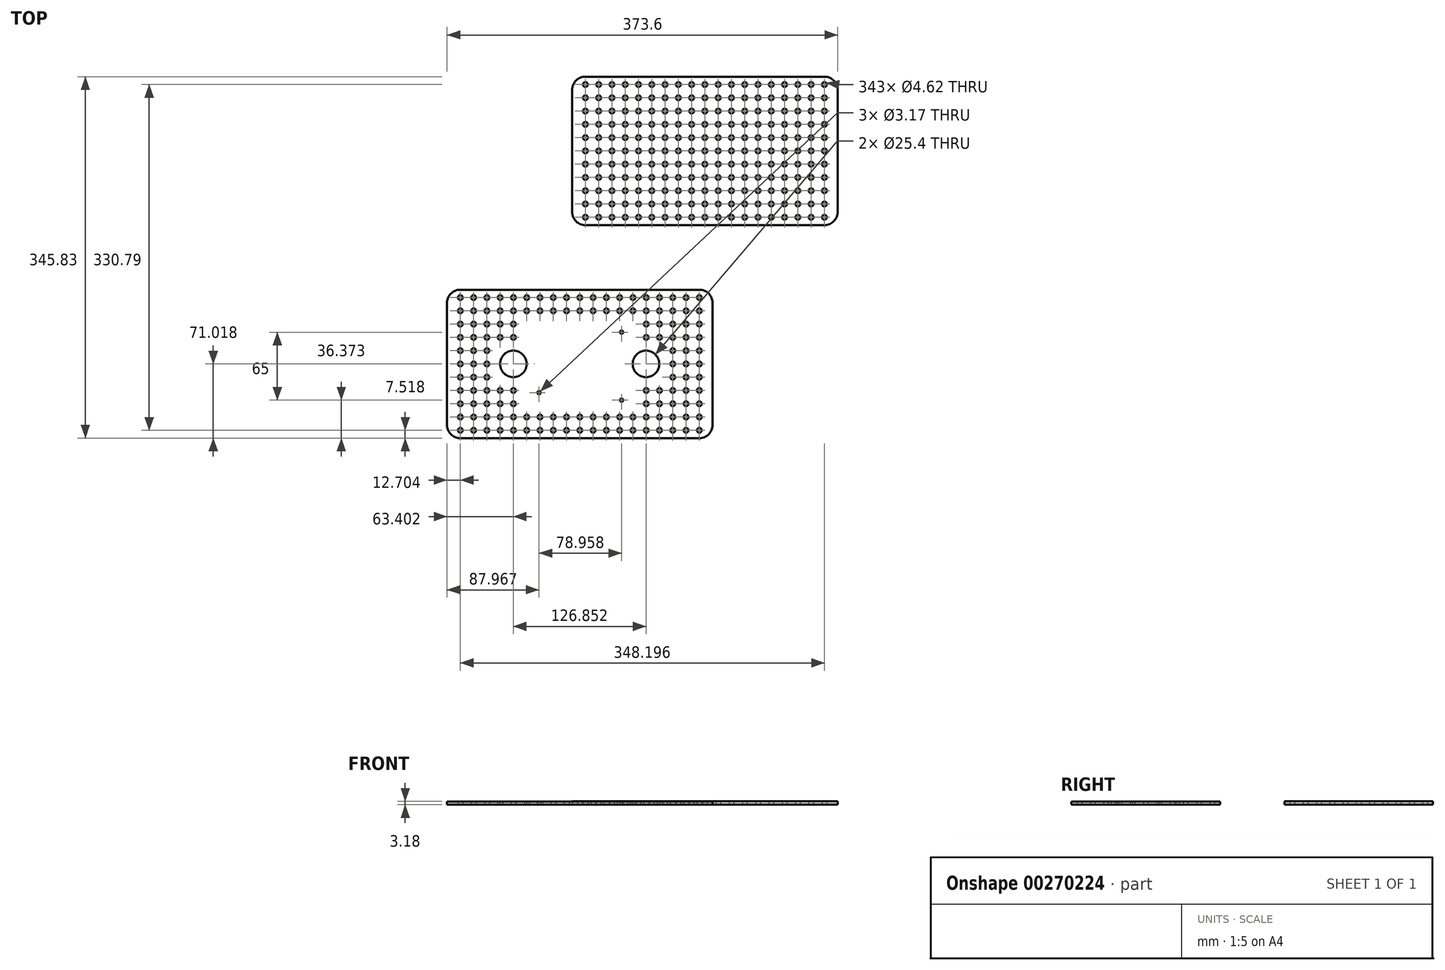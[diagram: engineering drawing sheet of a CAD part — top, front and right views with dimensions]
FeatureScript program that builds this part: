
annotation { "Feature Type Name" : "Feature", "Feature Type Description" : "" }
export const myFeature = defineFeature(function(context is Context, id is Id, definition is map)
    precondition{}
    {
        {
            var Q0;
            Q0=qCreatedBy(makeId("Top.planeOp"),FACE);
            var sketch = newSketch(context, id + "F0", { "sketchPlane" : qUnion([Q0])});
            skLineSegment(sketch, "E0.bottom", {"start": v(12.7, 0) * mm, "end": v(241.3, 0) * mm});
            skLineSegment(sketch, "E0.top", {"start": v(12.7, 142.04) * mm, "end": v(241.3, 142.04) * mm});
            skLineSegment(sketch, "E0.left", {"start": v(0, 12.7) * mm, "end": v(0, 129.34) * mm});
            skLineSegment(sketch, "E0.right", {"start": v(254, 12.7) * mm, "end": v(254, 129.34) * mm});
            skCircle(sketch, "E1", {"center": v(12.7, 134.52) * mm, "radius": 2.31 * mm});
            skCircle(sketch, "E2.1.0.0", {"center": v(25.4, 134.52) * mm, "radius": 2.31 * mm});
            skCircle(sketch, "E2.2.0.0", {"center": v(38.1, 134.52) * mm, "radius": 2.31 * mm});
            skCircle(sketch, "E2.3.0.0", {"center": v(50.8, 134.52) * mm, "radius": 2.31 * mm});
            skCircle(sketch, "E2.4.0.0", {"center": v(63.5, 134.52) * mm, "radius": 2.31 * mm});
            skCircle(sketch, "E2.5.0.0", {"center": v(76.2, 134.52) * mm, "radius": 2.31 * mm});
            skCircle(sketch, "E2.6.0.0", {"center": v(88.9, 134.52) * mm, "radius": 2.31 * mm});
            skCircle(sketch, "E2.7.0.0", {"center": v(101.6, 134.52) * mm, "radius": 2.31 * mm});
            skCircle(sketch, "E2.8.0.0", {"center": v(114.3, 134.52) * mm, "radius": 2.31 * mm});
            skCircle(sketch, "E2.9.0.0", {"center": v(127, 134.52) * mm, "radius": 2.31 * mm});
            skCircle(sketch, "E2.10.0.0", {"center": v(139.7, 134.52) * mm, "radius": 2.31 * mm});
            skLineSegment(sketch, "E2.direction1", {"start": v(12.7, 134.52) * mm, "end": v(25.4, 134.52) * mm, "construction": true});
            skCircle(sketch, "E3.0.11.0", {"center": v(152.4, 134.52) * mm, "radius": 2.31 * mm});
            skCircle(sketch, "E3.0.12.0", {"center": v(165.1, 134.52) * mm, "radius": 2.31 * mm});
            skCircle(sketch, "E3.0.13.0", {"center": v(177.8, 134.52) * mm, "radius": 2.31 * mm});
            skCircle(sketch, "E3.0.14.0", {"center": v(190.5, 134.52) * mm, "radius": 2.31 * mm});
            skCircle(sketch, "E3.0.15.0", {"center": v(203.2, 134.52) * mm, "radius": 2.31 * mm});
            skCircle(sketch, "E3.0.16.0", {"center": v(215.9, 134.52) * mm, "radius": 2.31 * mm});
            skCircle(sketch, "E3.0.17.0", {"center": v(228.6, 134.52) * mm, "radius": 2.31 * mm});
            skCircle(sketch, "E3.0.18.0", {"center": v(241.3, 134.52) * mm, "radius": 2.31 * mm});
            skCircle(sketch, "E4.0.1.0", {"center": v(76.2, 121.82) * mm, "radius": 2.31 * mm});
            skCircle(sketch, "E4.0.2.0", {"center": v(76.2, 109.12) * mm, "radius": 2.31 * mm});
            skCircle(sketch, "E4.0.3.0", {"center": v(76.2, 96.42) * mm, "radius": 2.31 * mm});
            skCircle(sketch, "E4.0.4.0", {"center": v(76.2, 83.72) * mm, "radius": 2.31 * mm});
            skCircle(sketch, "E4.0.5.0", {"center": v(76.2, 71.02) * mm, "radius": 2.31 * mm});
            skCircle(sketch, "E4.0.6.0", {"center": v(76.2, 58.32) * mm, "radius": 2.31 * mm});
            skCircle(sketch, "E4.0.7.0", {"center": v(76.2, 45.62) * mm, "radius": 2.31 * mm});
            skCircle(sketch, "E4.0.8.0", {"center": v(76.2, 32.92) * mm, "radius": 2.31 * mm});
            skCircle(sketch, "E4.0.9.0", {"center": v(76.2, 20.22) * mm, "radius": 2.31 * mm});
            skCircle(sketch, "E4.0.10.0", {"center": v(76.2, 7.52) * mm, "radius": 2.31 * mm});
            skCircle(sketch, "E4.1.1.0", {"center": v(88.9, 121.82) * mm, "radius": 2.31 * mm});
            skCircle(sketch, "E4.1.2.0", {"center": v(88.9, 109.12) * mm, "radius": 2.31 * mm});
            skCircle(sketch, "E4.1.3.0", {"center": v(88.9, 96.42) * mm, "radius": 2.31 * mm});
            skCircle(sketch, "E4.1.4.0", {"center": v(88.9, 83.72) * mm, "radius": 2.31 * mm});
            skCircle(sketch, "E4.1.5.0", {"center": v(88.9, 71.02) * mm, "radius": 2.31 * mm});
            skCircle(sketch, "E4.1.6.0", {"center": v(88.9, 58.32) * mm, "radius": 2.31 * mm});
            skCircle(sketch, "E4.1.7.0", {"center": v(88.9, 45.62) * mm, "radius": 2.31 * mm});
            skCircle(sketch, "E4.1.8.0", {"center": v(88.9, 32.92) * mm, "radius": 2.31 * mm});
            skCircle(sketch, "E4.1.9.0", {"center": v(88.9, 20.22) * mm, "radius": 2.31 * mm});
            skCircle(sketch, "E4.1.10.0", {"center": v(88.9, 7.52) * mm, "radius": 2.31 * mm});
            skCircle(sketch, "E4.2.1.0", {"center": v(101.6, 121.82) * mm, "radius": 2.31 * mm});
            skCircle(sketch, "E4.2.2.0", {"center": v(101.6, 109.12) * mm, "radius": 2.31 * mm});
            skCircle(sketch, "E4.2.3.0", {"center": v(101.6, 96.42) * mm, "radius": 2.31 * mm});
            skCircle(sketch, "E4.2.4.0", {"center": v(101.6, 83.72) * mm, "radius": 2.31 * mm});
            skCircle(sketch, "E4.2.5.0", {"center": v(101.6, 71.02) * mm, "radius": 2.31 * mm});
            skCircle(sketch, "E4.2.6.0", {"center": v(101.6, 58.32) * mm, "radius": 2.31 * mm});
            skCircle(sketch, "E4.2.7.0", {"center": v(101.6, 45.62) * mm, "radius": 2.31 * mm});
            skCircle(sketch, "E4.2.8.0", {"center": v(101.6, 32.92) * mm, "radius": 2.31 * mm});
            skCircle(sketch, "E4.2.9.0", {"center": v(101.6, 20.22) * mm, "radius": 2.31 * mm});
            skCircle(sketch, "E4.2.10.0", {"center": v(101.6, 7.52) * mm, "radius": 2.31 * mm});
            skCircle(sketch, "E4.3.1.0", {"center": v(114.3, 121.82) * mm, "radius": 2.31 * mm});
            skCircle(sketch, "E4.3.2.0", {"center": v(114.3, 109.12) * mm, "radius": 2.31 * mm});
            skCircle(sketch, "E4.3.3.0", {"center": v(114.3, 96.42) * mm, "radius": 2.31 * mm});
            skCircle(sketch, "E4.3.4.0", {"center": v(114.3, 83.72) * mm, "radius": 2.31 * mm});
            skCircle(sketch, "E4.3.5.0", {"center": v(114.3, 71.02) * mm, "radius": 2.31 * mm});
            skCircle(sketch, "E4.3.6.0", {"center": v(114.3, 58.32) * mm, "radius": 2.31 * mm});
            skCircle(sketch, "E4.3.7.0", {"center": v(114.3, 45.62) * mm, "radius": 2.31 * mm});
            skCircle(sketch, "E4.3.8.0", {"center": v(114.3, 32.92) * mm, "radius": 2.31 * mm});
            skCircle(sketch, "E4.3.9.0", {"center": v(114.3, 20.22) * mm, "radius": 2.31 * mm});
            skCircle(sketch, "E4.3.10.0", {"center": v(114.3, 7.52) * mm, "radius": 2.31 * mm});
            skCircle(sketch, "E4.4.1.0", {"center": v(127, 121.82) * mm, "radius": 2.31 * mm});
            skCircle(sketch, "E4.4.2.0", {"center": v(127, 109.12) * mm, "radius": 2.31 * mm});
            skCircle(sketch, "E4.4.3.0", {"center": v(127, 96.42) * mm, "radius": 2.31 * mm});
            skCircle(sketch, "E4.4.4.0", {"center": v(127, 83.72) * mm, "radius": 2.31 * mm});
            skCircle(sketch, "E4.4.5.0", {"center": v(127, 71.02) * mm, "radius": 2.31 * mm});
            skCircle(sketch, "E4.4.6.0", {"center": v(127, 58.32) * mm, "radius": 2.31 * mm});
            skCircle(sketch, "E4.4.7.0", {"center": v(127, 45.62) * mm, "radius": 2.31 * mm});
            skCircle(sketch, "E4.4.8.0", {"center": v(127, 32.92) * mm, "radius": 2.31 * mm});
            skCircle(sketch, "E4.4.9.0", {"center": v(127, 20.22) * mm, "radius": 2.31 * mm});
            skCircle(sketch, "E4.4.10.0", {"center": v(127, 7.52) * mm, "radius": 2.31 * mm});
            skCircle(sketch, "E4.5.1.0", {"center": v(139.7, 121.82) * mm, "radius": 2.31 * mm});
            skCircle(sketch, "E4.5.2.0", {"center": v(139.7, 109.12) * mm, "radius": 2.31 * mm});
            skCircle(sketch, "E4.5.3.0", {"center": v(139.7, 96.42) * mm, "radius": 2.31 * mm});
            skCircle(sketch, "E4.5.4.0", {"center": v(139.7, 83.72) * mm, "radius": 2.31 * mm});
            skCircle(sketch, "E4.5.5.0", {"center": v(139.7, 71.02) * mm, "radius": 2.31 * mm});
            skCircle(sketch, "E4.5.6.0", {"center": v(139.7, 58.32) * mm, "radius": 2.31 * mm});
            skCircle(sketch, "E4.5.7.0", {"center": v(139.7, 45.62) * mm, "radius": 2.31 * mm});
            skCircle(sketch, "E4.5.8.0", {"center": v(139.7, 32.92) * mm, "radius": 2.31 * mm});
            skCircle(sketch, "E4.5.9.0", {"center": v(139.7, 20.22) * mm, "radius": 2.31 * mm});
            skCircle(sketch, "E4.5.10.0", {"center": v(139.7, 7.52) * mm, "radius": 2.31 * mm});
            skCircle(sketch, "E4.6.1.0", {"center": v(152.4, 121.82) * mm, "radius": 2.31 * mm});
            skCircle(sketch, "E4.6.2.0", {"center": v(152.4, 109.12) * mm, "radius": 2.31 * mm});
            skCircle(sketch, "E4.6.3.0", {"center": v(152.4, 96.42) * mm, "radius": 2.31 * mm});
            skCircle(sketch, "E4.6.4.0", {"center": v(152.4, 83.72) * mm, "radius": 2.31 * mm});
            skCircle(sketch, "E4.6.5.0", {"center": v(152.4, 71.02) * mm, "radius": 2.31 * mm});
            skCircle(sketch, "E4.6.6.0", {"center": v(152.4, 58.32) * mm, "radius": 2.31 * mm});
            skCircle(sketch, "E4.6.7.0", {"center": v(152.4, 45.62) * mm, "radius": 2.31 * mm});
            skCircle(sketch, "E4.6.8.0", {"center": v(152.4, 32.92) * mm, "radius": 2.31 * mm});
            skCircle(sketch, "E4.6.9.0", {"center": v(152.4, 20.22) * mm, "radius": 2.31 * mm});
            skCircle(sketch, "E4.6.10.0", {"center": v(152.4, 7.52) * mm, "radius": 2.31 * mm});
            skCircle(sketch, "E4.7.1.0", {"center": v(165.1, 121.82) * mm, "radius": 2.31 * mm});
            skCircle(sketch, "E4.7.2.0", {"center": v(165.1, 109.12) * mm, "radius": 2.31 * mm});
            skCircle(sketch, "E4.7.3.0", {"center": v(165.1, 96.42) * mm, "radius": 2.31 * mm});
            skCircle(sketch, "E4.7.4.0", {"center": v(165.1, 83.72) * mm, "radius": 2.31 * mm});
            skCircle(sketch, "E4.7.5.0", {"center": v(165.1, 71.02) * mm, "radius": 2.31 * mm});
            skCircle(sketch, "E4.7.6.0", {"center": v(165.1, 58.32) * mm, "radius": 2.31 * mm});
            skCircle(sketch, "E4.7.7.0", {"center": v(165.1, 45.62) * mm, "radius": 2.31 * mm});
            skCircle(sketch, "E4.7.8.0", {"center": v(165.1, 32.92) * mm, "radius": 2.31 * mm});
            skCircle(sketch, "E4.7.9.0", {"center": v(165.1, 20.22) * mm, "radius": 2.31 * mm});
            skCircle(sketch, "E4.7.10.0", {"center": v(165.1, 7.52) * mm, "radius": 2.31 * mm});
            skCircle(sketch, "E4.8.1.0", {"center": v(177.8, 121.82) * mm, "radius": 2.31 * mm});
            skCircle(sketch, "E4.8.2.0", {"center": v(177.8, 109.12) * mm, "radius": 2.31 * mm});
            skCircle(sketch, "E4.8.3.0", {"center": v(177.8, 96.42) * mm, "radius": 2.31 * mm});
            skCircle(sketch, "E4.8.4.0", {"center": v(177.8, 83.72) * mm, "radius": 2.31 * mm});
            skCircle(sketch, "E4.8.5.0", {"center": v(177.8, 71.02) * mm, "radius": 2.31 * mm});
            skCircle(sketch, "E4.8.6.0", {"center": v(177.8, 58.32) * mm, "radius": 2.31 * mm});
            skCircle(sketch, "E4.8.7.0", {"center": v(177.8, 45.62) * mm, "radius": 2.31 * mm});
            skCircle(sketch, "E4.8.8.0", {"center": v(177.8, 32.92) * mm, "radius": 2.31 * mm});
            skCircle(sketch, "E4.8.9.0", {"center": v(177.8, 20.22) * mm, "radius": 2.31 * mm});
            skCircle(sketch, "E4.8.10.0", {"center": v(177.8, 7.52) * mm, "radius": 2.31 * mm});
            skCircle(sketch, "E4.9.1.0", {"center": v(190.5, 121.82) * mm, "radius": 2.31 * mm});
            skCircle(sketch, "E4.9.2.0", {"center": v(190.5, 109.12) * mm, "radius": 2.31 * mm});
            skCircle(sketch, "E4.9.3.0", {"center": v(190.5, 96.42) * mm, "radius": 2.31 * mm});
            skCircle(sketch, "E4.9.4.0", {"center": v(190.5, 83.72) * mm, "radius": 2.31 * mm});
            skCircle(sketch, "E4.9.5.0", {"center": v(190.5, 71.02) * mm, "radius": 2.31 * mm});
            skCircle(sketch, "E4.9.6.0", {"center": v(190.5, 58.32) * mm, "radius": 2.31 * mm});
            skCircle(sketch, "E4.9.7.0", {"center": v(190.5, 45.62) * mm, "radius": 2.31 * mm});
            skCircle(sketch, "E4.9.8.0", {"center": v(190.5, 32.92) * mm, "radius": 2.31 * mm});
            skCircle(sketch, "E4.9.9.0", {"center": v(190.5, 20.22) * mm, "radius": 2.31 * mm});
            skCircle(sketch, "E4.9.10.0", {"center": v(190.5, 7.52) * mm, "radius": 2.31 * mm});
            skCircle(sketch, "E4.10.1.0", {"center": v(203.2, 121.82) * mm, "radius": 2.31 * mm});
            skCircle(sketch, "E4.10.2.0", {"center": v(203.2, 109.12) * mm, "radius": 2.31 * mm});
            skCircle(sketch, "E4.10.3.0", {"center": v(203.2, 96.42) * mm, "radius": 2.31 * mm});
            skCircle(sketch, "E4.10.4.0", {"center": v(203.2, 83.72) * mm, "radius": 2.31 * mm});
            skCircle(sketch, "E4.10.5.0", {"center": v(203.2, 71.02) * mm, "radius": 2.31 * mm});
            skCircle(sketch, "E4.10.6.0", {"center": v(203.2, 58.32) * mm, "radius": 2.31 * mm});
            skCircle(sketch, "E4.10.7.0", {"center": v(203.2, 45.62) * mm, "radius": 2.31 * mm});
            skCircle(sketch, "E4.10.8.0", {"center": v(203.2, 32.92) * mm, "radius": 2.31 * mm});
            skCircle(sketch, "E4.10.9.0", {"center": v(203.2, 20.22) * mm, "radius": 2.31 * mm});
            skCircle(sketch, "E4.10.10.0", {"center": v(203.2, 7.52) * mm, "radius": 2.31 * mm});
            skCircle(sketch, "E4.11.1.0", {"center": v(215.9, 121.82) * mm, "radius": 2.31 * mm});
            skCircle(sketch, "E4.11.2.0", {"center": v(215.9, 109.12) * mm, "radius": 2.31 * mm});
            skCircle(sketch, "E4.11.3.0", {"center": v(215.9, 96.42) * mm, "radius": 2.31 * mm});
            skCircle(sketch, "E4.11.4.0", {"center": v(215.9, 83.72) * mm, "radius": 2.31 * mm});
            skCircle(sketch, "E4.11.5.0", {"center": v(215.9, 71.02) * mm, "radius": 2.31 * mm});
            skCircle(sketch, "E4.11.6.0", {"center": v(215.9, 58.32) * mm, "radius": 2.31 * mm});
            skCircle(sketch, "E4.11.7.0", {"center": v(215.9, 45.62) * mm, "radius": 2.31 * mm});
            skCircle(sketch, "E4.11.8.0", {"center": v(215.9, 32.92) * mm, "radius": 2.31 * mm});
            skCircle(sketch, "E4.11.9.0", {"center": v(215.9, 20.22) * mm, "radius": 2.31 * mm});
            skCircle(sketch, "E4.11.10.0", {"center": v(215.9, 7.52) * mm, "radius": 2.31 * mm});
            skCircle(sketch, "E4.12.1.0", {"center": v(228.6, 121.82) * mm, "radius": 2.31 * mm});
            skCircle(sketch, "E4.12.2.0", {"center": v(228.6, 109.12) * mm, "radius": 2.31 * mm});
            skCircle(sketch, "E4.12.3.0", {"center": v(228.6, 96.42) * mm, "radius": 2.31 * mm});
            skCircle(sketch, "E4.12.4.0", {"center": v(228.6, 83.72) * mm, "radius": 2.31 * mm});
            skCircle(sketch, "E4.12.5.0", {"center": v(228.6, 71.02) * mm, "radius": 2.31 * mm});
            skCircle(sketch, "E4.12.6.0", {"center": v(228.6, 58.32) * mm, "radius": 2.31 * mm});
            skCircle(sketch, "E4.12.7.0", {"center": v(228.6, 45.62) * mm, "radius": 2.31 * mm});
            skCircle(sketch, "E4.12.8.0", {"center": v(228.6, 32.92) * mm, "radius": 2.31 * mm});
            skCircle(sketch, "E4.12.9.0", {"center": v(228.6, 20.22) * mm, "radius": 2.31 * mm});
            skCircle(sketch, "E4.12.10.0", {"center": v(228.6, 7.52) * mm, "radius": 2.31 * mm});
            skCircle(sketch, "E4.13.1.0", {"center": v(241.3, 121.82) * mm, "radius": 2.31 * mm});
            skCircle(sketch, "E4.13.2.0", {"center": v(241.3, 109.12) * mm, "radius": 2.31 * mm});
            skCircle(sketch, "E4.13.3.0", {"center": v(241.3, 96.42) * mm, "radius": 2.31 * mm});
            skCircle(sketch, "E4.13.4.0", {"center": v(241.3, 83.72) * mm, "radius": 2.31 * mm});
            skCircle(sketch, "E4.13.5.0", {"center": v(241.3, 71.02) * mm, "radius": 2.31 * mm});
            skCircle(sketch, "E4.13.6.0", {"center": v(241.3, 58.32) * mm, "radius": 2.31 * mm});
            skCircle(sketch, "E4.13.7.0", {"center": v(241.3, 45.62) * mm, "radius": 2.31 * mm});
            skCircle(sketch, "E4.13.8.0", {"center": v(241.3, 32.92) * mm, "radius": 2.31 * mm});
            skCircle(sketch, "E4.13.9.0", {"center": v(241.3, 20.22) * mm, "radius": 2.31 * mm});
            skCircle(sketch, "E4.13.10.0", {"center": v(241.3, 7.52) * mm, "radius": 2.31 * mm});
            skLineSegment(sketch, "E4.direction1", {"start": v(76.2, 134.52) * mm, "end": v(88.9, 134.52) * mm, "construction": true});
            skLineSegment(sketch, "E4.direction2", {"start": v(76.2, 134.52) * mm, "end": v(76.2, 121.82) * mm, "construction": true});
            skCircle(sketch, "E5.0.1.0", {"center": v(12.7, 121.82) * mm, "radius": 2.31 * mm});
            skCircle(sketch, "E5.0.2.0", {"center": v(12.7, 109.12) * mm, "radius": 2.31 * mm});
            skCircle(sketch, "E5.0.3.0", {"center": v(12.7, 96.42) * mm, "radius": 2.31 * mm});
            skCircle(sketch, "E5.0.4.0", {"center": v(12.7, 83.72) * mm, "radius": 2.31 * mm});
            skCircle(sketch, "E5.0.5.0", {"center": v(12.7, 71.02) * mm, "radius": 2.31 * mm});
            skCircle(sketch, "E5.0.6.0", {"center": v(12.7, 58.32) * mm, "radius": 2.31 * mm});
            skCircle(sketch, "E5.0.7.0", {"center": v(12.7, 45.62) * mm, "radius": 2.31 * mm});
            skCircle(sketch, "E5.0.8.0", {"center": v(12.7, 32.92) * mm, "radius": 2.31 * mm});
            skCircle(sketch, "E5.0.9.0", {"center": v(12.7, 20.22) * mm, "radius": 2.31 * mm});
            skCircle(sketch, "E5.0.10.0", {"center": v(12.7, 7.52) * mm, "radius": 2.31 * mm});
            skCircle(sketch, "E5.1.1.0", {"center": v(25.4, 121.82) * mm, "radius": 2.31 * mm});
            skCircle(sketch, "E5.1.2.0", {"center": v(25.4, 109.12) * mm, "radius": 2.31 * mm});
            skCircle(sketch, "E5.1.3.0", {"center": v(25.4, 96.42) * mm, "radius": 2.31 * mm});
            skCircle(sketch, "E5.1.4.0", {"center": v(25.4, 83.72) * mm, "radius": 2.31 * mm});
            skCircle(sketch, "E5.1.5.0", {"center": v(25.4, 71.02) * mm, "radius": 2.31 * mm});
            skCircle(sketch, "E5.1.6.0", {"center": v(25.4, 58.32) * mm, "radius": 2.31 * mm});
            skCircle(sketch, "E5.1.7.0", {"center": v(25.4, 45.62) * mm, "radius": 2.31 * mm});
            skCircle(sketch, "E5.1.8.0", {"center": v(25.4, 32.92) * mm, "radius": 2.31 * mm});
            skCircle(sketch, "E5.1.9.0", {"center": v(25.4, 20.22) * mm, "radius": 2.31 * mm});
            skCircle(sketch, "E5.1.10.0", {"center": v(25.4, 7.52) * mm, "radius": 2.31 * mm});
            skCircle(sketch, "E5.2.1.0", {"center": v(38.1, 121.82) * mm, "radius": 2.31 * mm});
            skCircle(sketch, "E5.2.2.0", {"center": v(38.1, 109.12) * mm, "radius": 2.31 * mm});
            skCircle(sketch, "E5.2.3.0", {"center": v(38.1, 96.42) * mm, "radius": 2.31 * mm});
            skCircle(sketch, "E5.2.4.0", {"center": v(38.1, 83.72) * mm, "radius": 2.31 * mm});
            skCircle(sketch, "E5.2.5.0", {"center": v(38.1, 71.02) * mm, "radius": 2.31 * mm});
            skCircle(sketch, "E5.2.6.0", {"center": v(38.1, 58.32) * mm, "radius": 2.31 * mm});
            skCircle(sketch, "E5.2.7.0", {"center": v(38.1, 45.62) * mm, "radius": 2.31 * mm});
            skCircle(sketch, "E5.2.8.0", {"center": v(38.1, 32.92) * mm, "radius": 2.31 * mm});
            skCircle(sketch, "E5.2.9.0", {"center": v(38.1, 20.22) * mm, "radius": 2.31 * mm});
            skCircle(sketch, "E5.2.10.0", {"center": v(38.1, 7.52) * mm, "radius": 2.31 * mm});
            skCircle(sketch, "E5.3.1.0", {"center": v(50.8, 121.82) * mm, "radius": 2.31 * mm});
            skCircle(sketch, "E5.3.2.0", {"center": v(50.8, 109.12) * mm, "radius": 2.31 * mm});
            skCircle(sketch, "E5.3.3.0", {"center": v(50.8, 96.42) * mm, "radius": 2.31 * mm});
            skCircle(sketch, "E5.3.4.0", {"center": v(50.8, 83.72) * mm, "radius": 2.31 * mm});
            skCircle(sketch, "E5.3.5.0", {"center": v(50.8, 71.02) * mm, "radius": 2.31 * mm});
            skCircle(sketch, "E5.3.6.0", {"center": v(50.8, 58.32) * mm, "radius": 2.31 * mm});
            skCircle(sketch, "E5.3.7.0", {"center": v(50.8, 45.62) * mm, "radius": 2.31 * mm});
            skCircle(sketch, "E5.3.8.0", {"center": v(50.8, 32.92) * mm, "radius": 2.31 * mm});
            skCircle(sketch, "E5.3.9.0", {"center": v(50.8, 20.22) * mm, "radius": 2.31 * mm});
            skCircle(sketch, "E5.3.10.0", {"center": v(50.8, 7.52) * mm, "radius": 2.31 * mm});
            skCircle(sketch, "E5.4.1.0", {"center": v(63.5, 121.82) * mm, "radius": 2.31 * mm});
            skCircle(sketch, "E5.4.2.0", {"center": v(63.5, 109.12) * mm, "radius": 2.31 * mm});
            skCircle(sketch, "E5.4.3.0", {"center": v(63.5, 96.42) * mm, "radius": 2.31 * mm});
            skCircle(sketch, "E5.4.4.0", {"center": v(63.5, 83.72) * mm, "radius": 2.31 * mm});
            skCircle(sketch, "E5.4.5.0", {"center": v(63.5, 71.02) * mm, "radius": 2.31 * mm});
            skCircle(sketch, "E5.4.6.0", {"center": v(63.5, 58.32) * mm, "radius": 2.31 * mm});
            skCircle(sketch, "E5.4.7.0", {"center": v(63.5, 45.62) * mm, "radius": 2.31 * mm});
            skCircle(sketch, "E5.4.8.0", {"center": v(63.5, 32.92) * mm, "radius": 2.31 * mm});
            skCircle(sketch, "E5.4.9.0", {"center": v(63.5, 20.22) * mm, "radius": 2.31 * mm});
            skCircle(sketch, "E5.4.10.0", {"center": v(63.5, 7.52) * mm, "radius": 2.31 * mm});
            skLineSegment(sketch, "E5.direction2", {"start": v(12.7, 134.52) * mm, "end": v(12.7, 121.82) * mm, "construction": true});
            skLineSegment(sketch, "E6.bottom", {"start": v(-106.9, -203.8) * mm, "end": v(121.7, -203.8) * mm});
            skLineSegment(sketch, "E6.top", {"start": v(-106.9, -61.75) * mm, "end": v(121.7, -61.75) * mm});
            skLineSegment(sketch, "E6.left", {"start": v(-119.6, -191.1) * mm, "end": v(-119.6, -74.45) * mm});
            skLineSegment(sketch, "E6.right", {"start": v(134.4, -191.1) * mm, "end": v(134.4, -74.45) * mm});
            skCircle(sketch, "E7", {"center": v(-106.9, -69.27) * mm, "radius": 2.31 * mm});
            skCircle(sketch, "E8.1.0.0", {"center": v(-94.2, -69.27) * mm, "radius": 2.31 * mm});
            skCircle(sketch, "E8.2.0.0", {"center": v(-81.5, -69.27) * mm, "radius": 2.31 * mm});
            skCircle(sketch, "E8.3.0.0", {"center": v(-68.8, -69.27) * mm, "radius": 2.31 * mm});
            skCircle(sketch, "E8.4.0.0", {"center": v(-56.1, -69.27) * mm, "radius": 2.31 * mm});
            skCircle(sketch, "E8.5.0.0", {"center": v(-43.4, -69.27) * mm, "radius": 2.31 * mm});
            skCircle(sketch, "E8.6.0.0", {"center": v(-30.7, -69.27) * mm, "radius": 2.31 * mm});
            skCircle(sketch, "E8.7.0.0", {"center": v(-18, -69.27) * mm, "radius": 2.31 * mm});
            skCircle(sketch, "E8.8.0.0", {"center": v(-5.3, -69.27) * mm, "radius": 2.31 * mm});
            skCircle(sketch, "E8.9.0.0", {"center": v(7.4, -69.27) * mm, "radius": 2.31 * mm});
            skCircle(sketch, "E8.10.0.0", {"center": v(20.1, -69.27) * mm, "radius": 2.31 * mm});
            skLineSegment(sketch, "E8.direction1", {"start": v(-106.9, -69.27) * mm, "end": v(-94.2, -69.27) * mm, "construction": true});
            skCircle(sketch, "E9.0.11.0", {"center": v(32.8, -69.27) * mm, "radius": 2.31 * mm});
            skCircle(sketch, "E9.0.12.0", {"center": v(45.5, -69.27) * mm, "radius": 2.31 * mm});
            skCircle(sketch, "E9.0.13.0", {"center": v(58.2, -69.27) * mm, "radius": 2.31 * mm});
            skCircle(sketch, "E9.0.14.0", {"center": v(70.9, -69.27) * mm, "radius": 2.31 * mm});
            skCircle(sketch, "E9.0.15.0", {"center": v(83.6, -69.27) * mm, "radius": 2.31 * mm});
            skCircle(sketch, "E9.0.16.0", {"center": v(96.3, -69.27) * mm, "radius": 2.31 * mm});
            skCircle(sketch, "E9.0.17.0", {"center": v(109, -69.27) * mm, "radius": 2.31 * mm});
            skCircle(sketch, "E9.0.18.0", {"center": v(121.7, -69.27) * mm, "radius": 2.31 * mm});
            skCircle(sketch, "E10.0.1.0", {"center": v(-43.4, -81.97) * mm, "radius": 2.31 * mm});
            skCircle(sketch, "E10.0.9.0", {"center": v(-43.4, -183.57) * mm, "radius": 2.31 * mm});
            skCircle(sketch, "E10.0.10.0", {"center": v(-43.4, -196.27) * mm, "radius": 2.31 * mm});
            skCircle(sketch, "E10.1.1.0", {"center": v(-30.7, -81.97) * mm, "radius": 2.31 * mm});
            skCircle(sketch, "E10.1.9.0", {"center": v(-30.7, -183.57) * mm, "radius": 2.31 * mm});
            skCircle(sketch, "E10.1.10.0", {"center": v(-30.7, -196.27) * mm, "radius": 2.31 * mm});
            skCircle(sketch, "E10.2.1.0", {"center": v(-18, -81.97) * mm, "radius": 2.31 * mm});
            skCircle(sketch, "E10.2.9.0", {"center": v(-18, -183.57) * mm, "radius": 2.31 * mm});
            skCircle(sketch, "E10.2.10.0", {"center": v(-18, -196.27) * mm, "radius": 2.31 * mm});
            skCircle(sketch, "E10.3.1.0", {"center": v(-5.3, -81.97) * mm, "radius": 2.31 * mm});
            skCircle(sketch, "E10.3.9.0", {"center": v(-5.3, -183.57) * mm, "radius": 2.31 * mm});
            skCircle(sketch, "E10.3.10.0", {"center": v(-5.3, -196.27) * mm, "radius": 2.31 * mm});
            skCircle(sketch, "E10.4.1.0", {"center": v(7.4, -81.97) * mm, "radius": 2.31 * mm});
            skCircle(sketch, "E10.4.9.0", {"center": v(7.4, -183.57) * mm, "radius": 2.31 * mm});
            skCircle(sketch, "E10.4.10.0", {"center": v(7.4, -196.27) * mm, "radius": 2.31 * mm});
            skCircle(sketch, "E10.5.1.0", {"center": v(20.1, -81.97) * mm, "radius": 2.31 * mm});
            skCircle(sketch, "E10.5.9.0", {"center": v(20.1, -183.57) * mm, "radius": 2.31 * mm});
            skCircle(sketch, "E10.5.10.0", {"center": v(20.1, -196.27) * mm, "radius": 2.31 * mm});
            skCircle(sketch, "E10.6.1.0", {"center": v(32.8, -81.97) * mm, "radius": 2.31 * mm});
            skCircle(sketch, "E10.6.9.0", {"center": v(32.8, -183.57) * mm, "radius": 2.31 * mm});
            skCircle(sketch, "E10.6.10.0", {"center": v(32.8, -196.27) * mm, "radius": 2.31 * mm});
            skCircle(sketch, "E10.7.1.0", {"center": v(45.5, -81.97) * mm, "radius": 2.31 * mm});
            skCircle(sketch, "E10.7.9.0", {"center": v(45.5, -183.57) * mm, "radius": 2.31 * mm});
            skCircle(sketch, "E10.7.10.0", {"center": v(45.5, -196.27) * mm, "radius": 2.31 * mm});
            skCircle(sketch, "E10.8.1.0", {"center": v(58.2, -81.97) * mm, "radius": 2.31 * mm});
            skCircle(sketch, "E10.8.9.0", {"center": v(58.2, -183.57) * mm, "radius": 2.31 * mm});
            skCircle(sketch, "E10.8.10.0", {"center": v(58.2, -196.27) * mm, "radius": 2.31 * mm});
            skCircle(sketch, "E10.9.1.0", {"center": v(70.9, -81.97) * mm, "radius": 2.31 * mm});
            skCircle(sketch, "E10.9.2.0", {"center": v(70.9, -94.67) * mm, "radius": 2.31 * mm});
            skCircle(sketch, "E10.9.3.0", {"center": v(70.9, -107.37) * mm, "radius": 2.31 * mm});
            skCircle(sketch, "E10.9.7.0", {"center": v(70.9, -158.17) * mm, "radius": 2.31 * mm});
            skCircle(sketch, "E10.9.8.0", {"center": v(70.9, -170.87) * mm, "radius": 2.31 * mm});
            skCircle(sketch, "E10.9.9.0", {"center": v(70.9, -183.57) * mm, "radius": 2.31 * mm});
            skCircle(sketch, "E10.9.10.0", {"center": v(70.9, -196.27) * mm, "radius": 2.31 * mm});
            skCircle(sketch, "E10.10.1.0", {"center": v(83.6, -81.97) * mm, "radius": 2.31 * mm});
            skCircle(sketch, "E10.10.2.0", {"center": v(83.6, -94.67) * mm, "radius": 2.31 * mm});
            skCircle(sketch, "E10.10.3.0", {"center": v(83.6, -107.37) * mm, "radius": 2.31 * mm});
            skCircle(sketch, "E10.10.7.0", {"center": v(83.6, -158.17) * mm, "radius": 2.31 * mm});
            skCircle(sketch, "E10.10.8.0", {"center": v(83.6, -170.87) * mm, "radius": 2.31 * mm});
            skCircle(sketch, "E10.10.9.0", {"center": v(83.6, -183.57) * mm, "radius": 2.31 * mm});
            skCircle(sketch, "E10.10.10.0", {"center": v(83.6, -196.27) * mm, "radius": 2.31 * mm});
            skCircle(sketch, "E10.11.1.0", {"center": v(96.3, -81.97) * mm, "radius": 2.31 * mm});
            skCircle(sketch, "E10.11.2.0", {"center": v(96.3, -94.67) * mm, "radius": 2.31 * mm});
            skCircle(sketch, "E10.11.3.0", {"center": v(96.3, -107.37) * mm, "radius": 2.31 * mm});
            skCircle(sketch, "E10.11.4.0", {"center": v(96.3, -120.07) * mm, "radius": 2.31 * mm});
            skCircle(sketch, "E10.11.5.0", {"center": v(96.3, -132.77) * mm, "radius": 2.31 * mm});
            skCircle(sketch, "E10.11.6.0", {"center": v(96.3, -145.47) * mm, "radius": 2.31 * mm});
            skCircle(sketch, "E10.11.7.0", {"center": v(96.3, -158.17) * mm, "radius": 2.31 * mm});
            skCircle(sketch, "E10.11.8.0", {"center": v(96.3, -170.87) * mm, "radius": 2.31 * mm});
            skCircle(sketch, "E10.11.9.0", {"center": v(96.3, -183.57) * mm, "radius": 2.31 * mm});
            skCircle(sketch, "E10.11.10.0", {"center": v(96.3, -196.27) * mm, "radius": 2.31 * mm});
            skCircle(sketch, "E10.12.1.0", {"center": v(109, -81.97) * mm, "radius": 2.31 * mm});
            skCircle(sketch, "E10.12.2.0", {"center": v(109, -94.67) * mm, "radius": 2.31 * mm});
            skCircle(sketch, "E10.12.3.0", {"center": v(109, -107.37) * mm, "radius": 2.31 * mm});
            skCircle(sketch, "E10.12.4.0", {"center": v(109, -120.07) * mm, "radius": 2.31 * mm});
            skCircle(sketch, "E10.12.5.0", {"center": v(109, -132.77) * mm, "radius": 2.31 * mm});
            skCircle(sketch, "E10.12.6.0", {"center": v(109, -145.47) * mm, "radius": 2.31 * mm});
            skCircle(sketch, "E10.12.7.0", {"center": v(109, -158.17) * mm, "radius": 2.31 * mm});
            skCircle(sketch, "E10.12.8.0", {"center": v(109, -170.87) * mm, "radius": 2.31 * mm});
            skCircle(sketch, "E10.12.9.0", {"center": v(109, -183.57) * mm, "radius": 2.31 * mm});
            skCircle(sketch, "E10.12.10.0", {"center": v(109, -196.27) * mm, "radius": 2.31 * mm});
            skCircle(sketch, "E10.13.1.0", {"center": v(121.7, -81.97) * mm, "radius": 2.31 * mm});
            skCircle(sketch, "E10.13.2.0", {"center": v(121.7, -94.67) * mm, "radius": 2.31 * mm});
            skCircle(sketch, "E10.13.3.0", {"center": v(121.7, -107.37) * mm, "radius": 2.31 * mm});
            skCircle(sketch, "E10.13.4.0", {"center": v(121.7, -120.07) * mm, "radius": 2.31 * mm});
            skCircle(sketch, "E10.13.5.0", {"center": v(121.7, -132.77) * mm, "radius": 2.31 * mm});
            skCircle(sketch, "E10.13.6.0", {"center": v(121.7, -145.47) * mm, "radius": 2.31 * mm});
            skCircle(sketch, "E10.13.7.0", {"center": v(121.7, -158.17) * mm, "radius": 2.31 * mm});
            skCircle(sketch, "E10.13.8.0", {"center": v(121.7, -170.87) * mm, "radius": 2.31 * mm});
            skCircle(sketch, "E10.13.9.0", {"center": v(121.7, -183.57) * mm, "radius": 2.31 * mm});
            skCircle(sketch, "E10.13.10.0", {"center": v(121.7, -196.27) * mm, "radius": 2.31 * mm});
            skLineSegment(sketch, "E10.direction1", {"start": v(-43.4, -69.27) * mm, "end": v(-30.7, -69.27) * mm, "construction": true});
            skLineSegment(sketch, "E10.direction2", {"start": v(-43.4, -69.27) * mm, "end": v(-43.4, -81.97) * mm, "construction": true});
            skCircle(sketch, "E11.0.1.0", {"center": v(-106.9, -81.97) * mm, "radius": 2.31 * mm});
            skCircle(sketch, "E11.0.2.0", {"center": v(-106.9, -94.67) * mm, "radius": 2.31 * mm});
            skCircle(sketch, "E11.0.3.0", {"center": v(-106.9, -107.37) * mm, "radius": 2.31 * mm});
            skCircle(sketch, "E11.0.4.0", {"center": v(-106.9, -120.07) * mm, "radius": 2.31 * mm});
            skCircle(sketch, "E11.0.5.0", {"center": v(-106.9, -132.77) * mm, "radius": 2.31 * mm});
            skCircle(sketch, "E11.0.6.0", {"center": v(-106.9, -145.47) * mm, "radius": 2.31 * mm});
            skCircle(sketch, "E11.0.7.0", {"center": v(-106.9, -158.17) * mm, "radius": 2.31 * mm});
            skCircle(sketch, "E11.0.8.0", {"center": v(-106.9, -170.87) * mm, "radius": 2.31 * mm});
            skCircle(sketch, "E11.0.9.0", {"center": v(-106.9, -183.57) * mm, "radius": 2.31 * mm});
            skCircle(sketch, "E11.0.10.0", {"center": v(-106.9, -196.27) * mm, "radius": 2.31 * mm});
            skCircle(sketch, "E11.1.1.0", {"center": v(-94.2, -81.97) * mm, "radius": 2.31 * mm});
            skCircle(sketch, "E11.1.2.0", {"center": v(-94.2, -94.67) * mm, "radius": 2.31 * mm});
            skCircle(sketch, "E11.1.3.0", {"center": v(-94.2, -107.37) * mm, "radius": 2.31 * mm});
            skCircle(sketch, "E11.1.4.0", {"center": v(-94.2, -120.07) * mm, "radius": 2.31 * mm});
            skCircle(sketch, "E11.1.5.0", {"center": v(-94.2, -132.77) * mm, "radius": 2.31 * mm});
            skCircle(sketch, "E11.1.6.0", {"center": v(-94.2, -145.47) * mm, "radius": 2.31 * mm});
            skCircle(sketch, "E11.1.7.0", {"center": v(-94.2, -158.17) * mm, "radius": 2.31 * mm});
            skCircle(sketch, "E11.1.8.0", {"center": v(-94.2, -170.87) * mm, "radius": 2.31 * mm});
            skCircle(sketch, "E11.1.9.0", {"center": v(-94.2, -183.57) * mm, "radius": 2.31 * mm});
            skCircle(sketch, "E11.1.10.0", {"center": v(-94.2, -196.27) * mm, "radius": 2.31 * mm});
            skCircle(sketch, "E11.2.1.0", {"center": v(-81.5, -81.97) * mm, "radius": 2.31 * mm});
            skCircle(sketch, "E11.2.2.0", {"center": v(-81.5, -94.67) * mm, "radius": 2.31 * mm});
            skCircle(sketch, "E11.2.3.0", {"center": v(-81.5, -107.37) * mm, "radius": 2.31 * mm});
            skCircle(sketch, "E11.2.4.0", {"center": v(-81.5, -120.07) * mm, "radius": 2.31 * mm});
            skCircle(sketch, "E11.2.5.0", {"center": v(-81.5, -132.77) * mm, "radius": 2.31 * mm});
            skCircle(sketch, "E11.2.6.0", {"center": v(-81.5, -145.47) * mm, "radius": 2.31 * mm});
            skCircle(sketch, "E11.2.7.0", {"center": v(-81.5, -158.17) * mm, "radius": 2.31 * mm});
            skCircle(sketch, "E11.2.8.0", {"center": v(-81.5, -170.87) * mm, "radius": 2.31 * mm});
            skCircle(sketch, "E11.2.9.0", {"center": v(-81.5, -183.57) * mm, "radius": 2.31 * mm});
            skCircle(sketch, "E11.2.10.0", {"center": v(-81.5, -196.27) * mm, "radius": 2.31 * mm});
            skCircle(sketch, "E11.3.1.0", {"center": v(-68.8, -81.97) * mm, "radius": 2.31 * mm});
            skCircle(sketch, "E11.3.2.0", {"center": v(-68.8, -94.67) * mm, "radius": 2.31 * mm});
            skCircle(sketch, "E11.3.3.0", {"center": v(-68.8, -107.37) * mm, "radius": 2.31 * mm});
            skCircle(sketch, "E11.3.7.0", {"center": v(-68.8, -158.17) * mm, "radius": 2.31 * mm});
            skCircle(sketch, "E11.3.8.0", {"center": v(-68.8, -170.87) * mm, "radius": 2.31 * mm});
            skCircle(sketch, "E11.3.9.0", {"center": v(-68.8, -183.57) * mm, "radius": 2.31 * mm});
            skCircle(sketch, "E11.3.10.0", {"center": v(-68.8, -196.27) * mm, "radius": 2.31 * mm});
            skCircle(sketch, "E11.4.1.0", {"center": v(-56.1, -81.97) * mm, "radius": 2.31 * mm});
            skCircle(sketch, "E11.4.2.0", {"center": v(-56.1, -94.67) * mm, "radius": 2.31 * mm});
            skCircle(sketch, "E11.4.3.0", {"center": v(-56.1, -107.37) * mm, "radius": 2.31 * mm});
            skCircle(sketch, "E11.4.7.0", {"center": v(-56.1, -158.17) * mm, "radius": 2.31 * mm});
            skCircle(sketch, "E11.4.8.0", {"center": v(-56.1, -170.87) * mm, "radius": 2.31 * mm});
            skCircle(sketch, "E11.4.9.0", {"center": v(-56.1, -183.57) * mm, "radius": 2.31 * mm});
            skCircle(sketch, "E11.4.10.0", {"center": v(-56.1, -196.27) * mm, "radius": 2.31 * mm});
            skLineSegment(sketch, "E11.direction2", {"start": v(-106.9, -69.27) * mm, "end": v(-106.9, -81.97) * mm, "construction": true});
            skLineSegment(sketch, "E12.bottom", {"start": v(-37.72, -90.37) * mm, "end": v(52.53, -90.37) * mm});
            skLineSegment(sketch, "E12.top", {"start": v(-37.72, -175.17) * mm, "end": v(52.53, -175.17) * mm});
            skLineSegment(sketch, "E12.left", {"start": v(-37.72, -90.37) * mm, "end": v(-37.72, -175.17) * mm});
            skLineSegment(sketch, "E12.right", {"start": v(52.53, -90.37) * mm, "end": v(52.53, -175.17) * mm});
            skPoint(sketch, "E13", {"position": v(7.4, -90.37) * mm});
            skCircle(sketch, "E14", {"center": v(-56.2, -132.77) * mm, "radius": 12.7 * mm});
            skCircle(sketch, "E15", {"center": v(70.65, -132.77) * mm, "radius": 12.7 * mm});
            skPoint(sketch, "E16.visualSharp", {"position": v(254, 142.04) * mm});
            skArc(sketch, "E16.filletArc", {"start": v(254, 129.34) * mm, "mid": v(250.28, 138.32) * mm, "end": v(241.3, 142.04) * mm});
            skPoint(sketch, "E17.visualSharp", {"position": v(254, 0) * mm});
            skArc(sketch, "E17.filletArc", {"start": v(241.3, 0) * mm, "mid": v(250.28, 3.72) * mm, "end": v(254, 12.7) * mm});
            skPoint(sketch, "E18.visualSharp", {"position": v(0, 142.04) * mm});
            skArc(sketch, "E18.filletArc", {"start": v(12.7, 142.04) * mm, "mid": v(3.72, 138.32) * mm, "end": v(0, 129.34) * mm});
            skPoint(sketch, "E19.visualSharp", {"position": v(0, 0) * mm});
            skArc(sketch, "E19.filletArc", {"start": v(0, 12.7) * mm, "mid": v(3.72, 3.72) * mm, "end": v(12.7, 0) * mm});
            skPoint(sketch, "E20.visualSharp", {"position": v(134.4, -61.75) * mm});
            skArc(sketch, "E20.filletArc", {"start": v(134.4, -74.45) * mm, "mid": v(130.68, -65.47) * mm, "end": v(121.7, -61.75) * mm});
            skPoint(sketch, "E21.visualSharp", {"position": v(-119.6, -61.75) * mm});
            skArc(sketch, "E21.filletArc", {"start": v(-106.9, -61.75) * mm, "mid": v(-115.88, -65.47) * mm, "end": v(-119.6, -74.45) * mm});
            skPoint(sketch, "E22.visualSharp", {"position": v(-119.6, -203.8) * mm});
            skArc(sketch, "E22.filletArc", {"start": v(-119.6, -191.1) * mm, "mid": v(-115.88, -200.07) * mm, "end": v(-106.9, -203.8) * mm});
            skPoint(sketch, "E23.visualSharp", {"position": v(134.4, -203.8) * mm});
            skArc(sketch, "E23.filletArc", {"start": v(121.7, -203.8) * mm, "mid": v(130.68, -200.07) * mm, "end": v(134.4, -191.1) * mm});
            skCircle(sketch, "E24", {"center": v(47.32, -102.42) * mm, "radius": 1.59 * mm});
            skCircle(sketch, "E25", {"center": v(47.32, -167.42) * mm, "radius": 1.59 * mm});
            skPoint(sketch, "E26", {"position": v(134.4, -132.77) * mm});
            skPoint(sketch, "E27", {"position": v(52.53, -132.77) * mm});
            skCircle(sketch, "E28", {"center": v(-31.63, -160.23) * mm, "radius": 1.59 * mm});
            skSolve(sketch);
        }
        {
            var Q0;
            Q0=makeQuery(id+"F0.imprint","IMPRINT",FACE,{"disambiguationData":[TD([[makeQuery(id+"F0.imprint","IMPRINT",EDGE,{"derivedFrom":sQuery(id+"F0.wireOp",EDGE,"E0.bottom")}),1.0]])]});
            extrude(context, id + "F1", {"entities" : qUnion([Q0]), "depth" : 3.17 * mm});
        }
        {
            var Q0;
            Q0=makeQuery(id+"F0.imprint","IMPRINT",FACE,{"disambiguationData":[TD([[makeQuery(id+"F0.imprint","IMPRINT",EDGE,{"derivedFrom":sQuery(id+"F0.wireOp",EDGE,"E12.bottom")}),-1.0]])]});
            var Q1;
            Q1=makeQuery(id+"F0.imprint","IMPRINT",FACE,{"disambiguationData":[TD([[makeQuery(id+"F0.imprint","IMPRINT",EDGE,{"derivedFrom":sQuery(id+"F0.wireOp",EDGE,"E6.bottom")}),1.0]])]});
            extrude(context, id + "F2", {"entities" : qUnion([Q0, Q1]), "depth" : 3 * mm});
        }
    });
